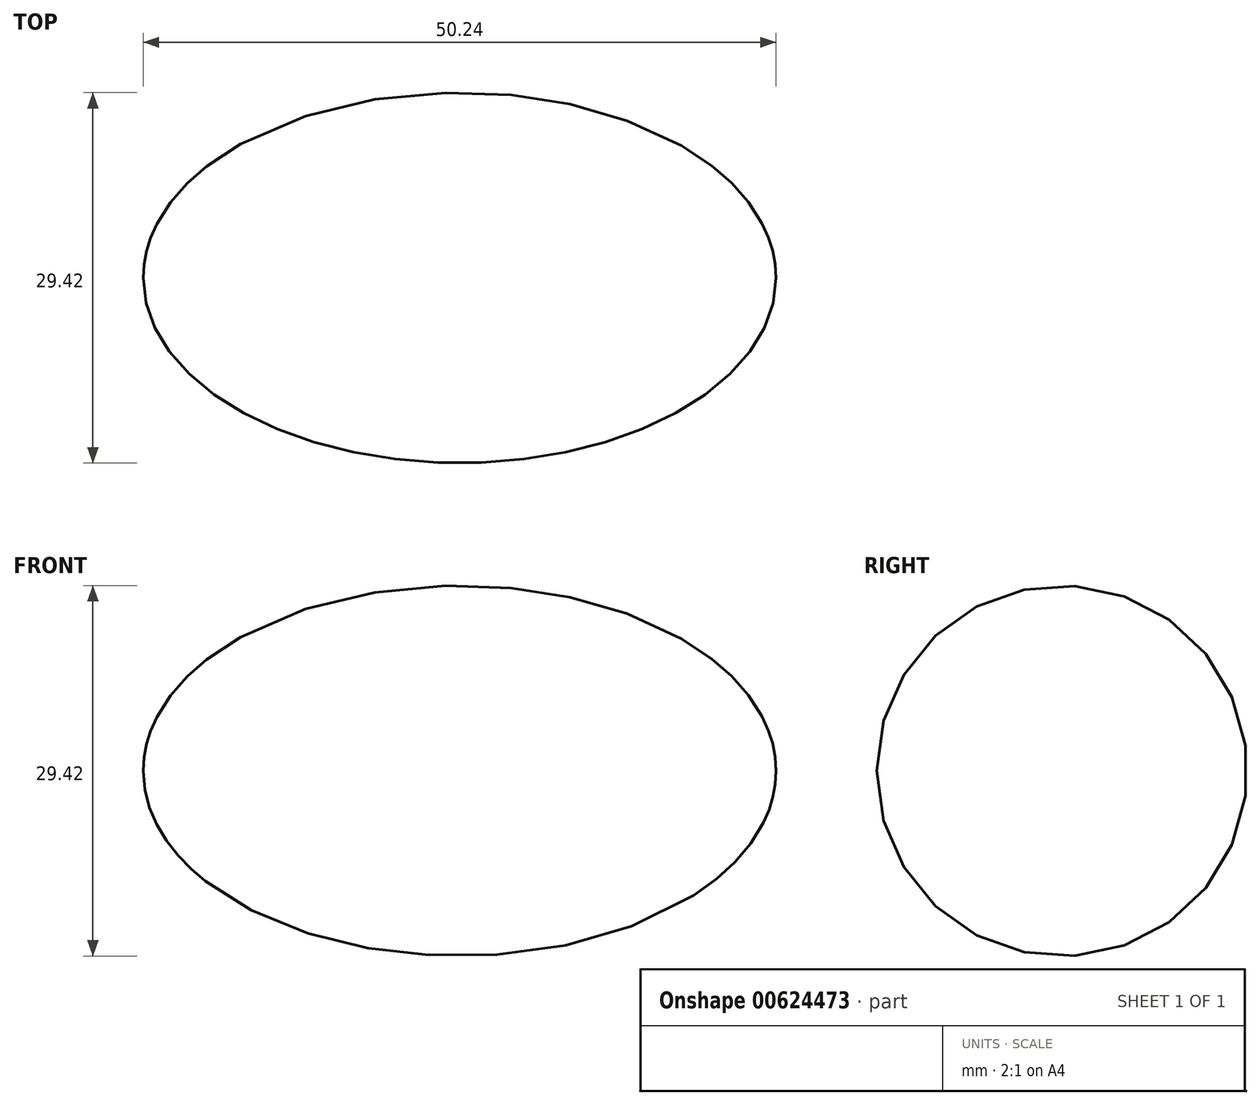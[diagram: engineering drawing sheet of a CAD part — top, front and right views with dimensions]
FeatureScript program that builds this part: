
annotation { "Feature Type Name" : "Feature", "Feature Type Description" : "" }
export const myFeature = defineFeature(function(context is Context, id is Id, definition is map)
    precondition{}
    {
        {
            var Q0;
            Q0=qCreatedBy(makeId("Top.planeOp"),FACE);
            var sketch = newSketch(context, id + "F0", { "sketchPlane" : qUnion([Q0])});
            skEllipse(sketch, "E0", {"center": v(0, 0) * mm, "majorRadius": 25.12 * mm, "minorRadius": 14.71 * mm, "majorAxis": v(1, 0)});
            skLineSegment(sketch, "E1", {"start": v(-70.44, 0) * mm, "end": v(71.53, 0) * mm});
            skSolve(sketch);
        }
        {
            var Q0;
            {var subQ0=sQuery(id+"F0.wireOp",EDGE,"E1");var subQ1=sQuery(id+"F0.wireOp",EDGE,"E0");var subQ2=makeQuery(id+"F0.imprint","INTERSECT",VERTEX,{"disambiguationData":[OD(0.0)],"derivedFrom":[subQ1,subQ0]});Q0=makeQuery(id+"F0.imprint","IMPRINT",FACE,{"disambiguationData":[TD([[makeQuery(id+"F0.imprint","IMPRINT",EDGE,{"disambiguationData":[TD([[subQ2,1.0]])],"derivedFrom":subQ1}),1.0]])]});}
            var Q1;
            Q1=sQuery(id+"F0.wireOp",EDGE,"E1");
            revolve(context, id + "F1", {"entities" : qUnion([Q0]), "axis" : qUnion([Q1]), "revolveType" : RevolveType.FULL});
        }
    });
